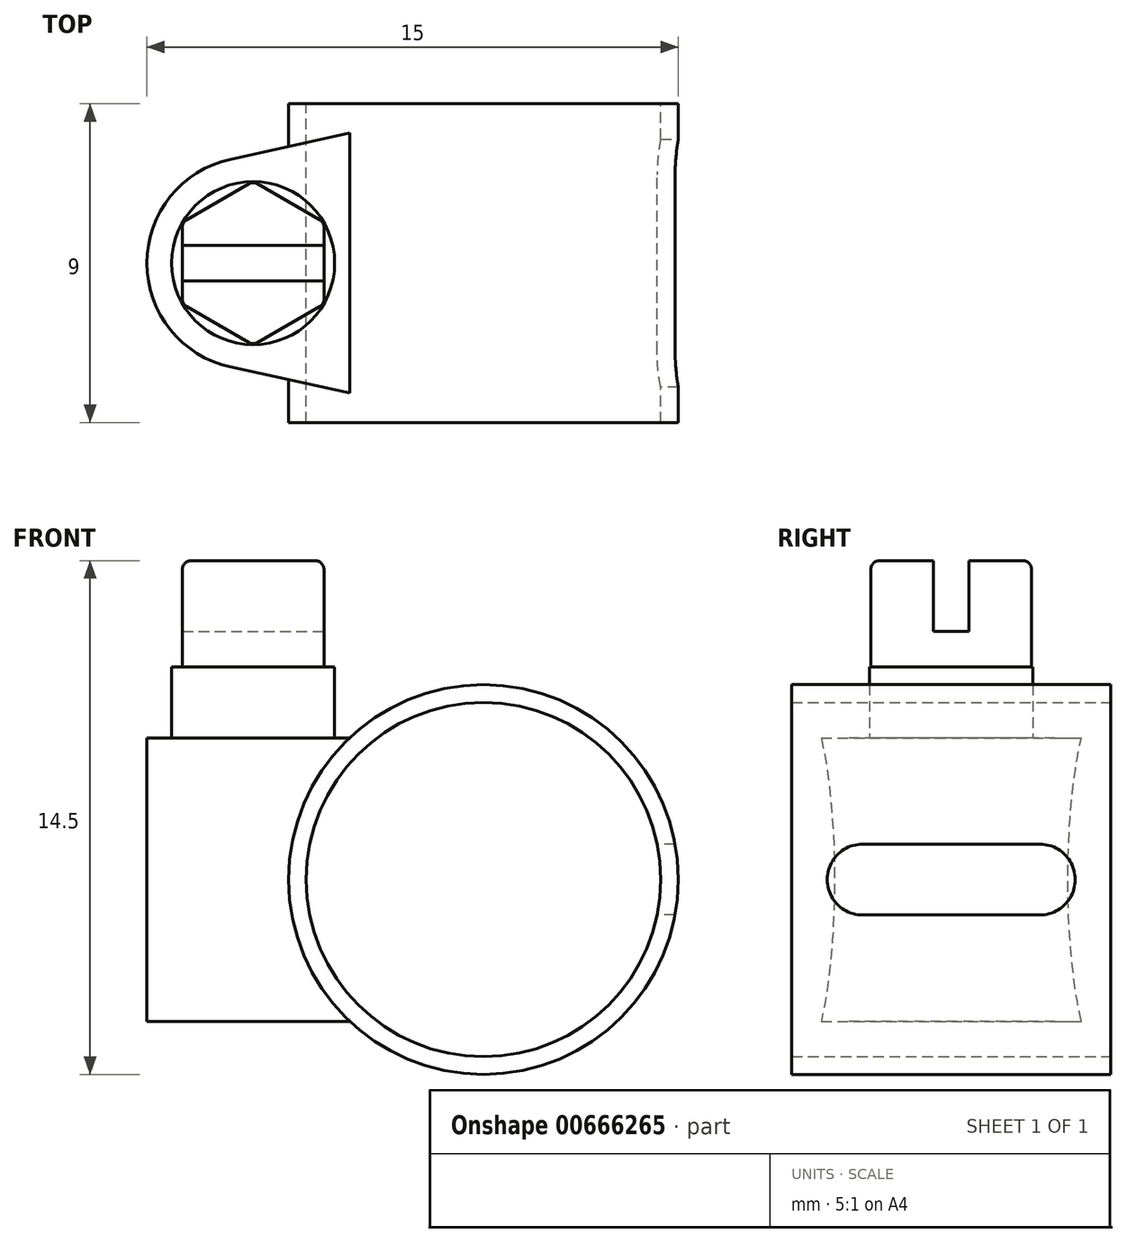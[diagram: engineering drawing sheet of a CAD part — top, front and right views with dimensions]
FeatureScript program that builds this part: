
annotation { "Feature Type Name" : "Feature", "Feature Type Description" : "" }
export const myFeature = defineFeature(function(context is Context, id is Id, definition is map)
    precondition{}
    {
        {
            var Q0;
            Q0=qCreatedBy(makeId("Front.planeOp"),FACE);
            var sketch = newSketch(context, id + "F0", { "sketchPlane" : qUnion([Q0])});
            skCircle(sketch, "E0", {"center": v(0, 0) * mm, "radius": 5.5 * mm});
            skCircle(sketch, "E1", {"center": v(0, 0) * mm, "radius": 5 * mm, "construction": true});
            skSolve(sketch);
        }
        {
            var Q0;
            Q0 = qSketchRegion(id + "F0", true);
            extrude(context, id + "F1", {"entities" : qUnion([Q0]), "depth" : 9 * mm, "offsetDistance" : 25 * mm, "symmetric" : true});
        }
        {
            var Q0;
            Q0=qCreatedBy(makeId("Top.planeOp"),FACE);
            var sketch = newSketch(context, id + "F2", { "sketchPlane" : qUnion([Q0])});
            skArc(sketch, "E2", {"start": v(-7.14, 2.93) * mm, "mid": v(-9.5, 0) * mm, "end": v(-7.14, -2.93) * mm});
            skLineSegment(sketch, "E3", {"start": v(-7.14, 2.93) * mm, "end": v(0, 4.5) * mm});
            skLineSegment(sketch, "E4", {"start": v(0, 4.5) * mm, "end": v(0, -4.5) * mm});
            skLineSegment(sketch, "E5", {"start": v(0, -4.5) * mm, "end": v(-7.14, -2.93) * mm});
            skSolve(sketch);
        }
        {
            var Q0;
            Q0 = qSketchRegion(id + "F2", true);
            extrude(context, id + "F3", {"entities" : qUnion([Q0]), "operationType" : NewBodyOperationType.ADD, "depth" : 8 * mm, "offsetDistance" : 25 * mm, "symmetric" : true});
        }
        {
            var Q0;
            Q0=makeQuery(id+"F3.opExtrude","CAP_FACE",FACE,{"disambiguationData":[OSD([sQuery(id+"F2.wireOp",EDGE,"E2"),sQuery(id+"F2.wireOp",EDGE,"E3"),sQuery(id+"F2.wireOp",EDGE,"E4"),sQuery(id+"F2.wireOp",EDGE,"E5")])],"isStart":false});
            var sketch = newSketch(context, id + "F4", { "sketchPlane" : qUnion([Q0])});
            skCircle(sketch, "E6.cCircle", {"center": v(-6.5, 0) * mm, "radius": 2 * mm, "construction": true});
            skLineSegment(sketch, "E6.0", {"start": v(-8.5, -1.15) * mm, "end": v(-8.5, 1.15) * mm});
            skLineSegment(sketch, "E6.1", {"start": v(-8.5, 1.15) * mm, "end": v(-6.5, 2.3) * mm});
            skLineSegment(sketch, "E6.2", {"start": v(-6.5, 2.3) * mm, "end": v(-4.5, 1.15) * mm});
            skLineSegment(sketch, "E6.3", {"start": v(-4.5, 1.15) * mm, "end": v(-4.5, -1.15) * mm});
            skLineSegment(sketch, "E6.4", {"start": v(-4.5, -1.15) * mm, "end": v(-6.5, -2.3) * mm});
            skLineSegment(sketch, "E6.5", {"start": v(-6.5, -2.3) * mm, "end": v(-8.5, -1.15) * mm});
            skPoint(sketch, "E6.0.midPoint", {"position": v(-8.5, 0) * mm});
            skSolve(sketch);
        }
        {
            var Q0;
            Q0 = qSketchRegion(id + "F4", true);
            extrude(context, id + "F5", {"entities" : qUnion([Q0]), "operationType" : NewBodyOperationType.ADD, "depth" : 5 * mm, "offsetDistance" : 25 * mm});
        }
        {
            var Q0;
            Q0=makeQuery(id+"F1.opExtrude","CAP_FACE",FACE,{"disambiguationData":[OSD([sQuery(id+"F0.wireOp",EDGE,"E0")])],"isStart":true});
            var sketch = newSketch(context, id + "F6", { "sketchPlane" : qUnion([Q0])});
            skCircle(sketch, "E7", {"center": v(0, 0) * mm, "radius": 5 * mm});
            skSolve(sketch);
        }
        {
            var Q0;
            Q0 = qSketchRegion(id + "F6", true);
            extrude(context, id + "F7", {"entities" : qUnion([Q0]), "operationType" : NewBodyOperationType.REMOVE, "endBound" : BoundingType.THROUGH_ALL, "oppositeDirection" : true, "depth" : 25 * mm, "offsetDistance" : 25 * mm});
        }
        {
            var Q0;
            Q0=makeQuery(id+"F5.opExtrude","CAP_FACE",FACE,{"disambiguationData":[OSD([sQuery(id+"F4.wireOp",EDGE,"E6.0"),sQuery(id+"F4.wireOp",EDGE,"E6.1"),sQuery(id+"F4.wireOp",EDGE,"E6.2"),sQuery(id+"F4.wireOp",EDGE,"E6.3"),sQuery(id+"F4.wireOp",EDGE,"E6.4"),sQuery(id+"F4.wireOp",EDGE,"E6.5")])],"isStart":false});
            var sketch = newSketch(context, id + "F8", { "sketchPlane" : qUnion([Q0])});
            skLineSegment(sketch, "E8.bottom", {"start": v(-8.5, 0.5) * mm, "end": v(-4.5, 0.5) * mm});
            skLineSegment(sketch, "E8.top", {"start": v(-8.5, -0.5) * mm, "end": v(-4.5, -0.5) * mm});
            skLineSegment(sketch, "E8.left", {"start": v(-8.5, 0.5) * mm, "end": v(-8.5, -0.5) * mm});
            skLineSegment(sketch, "E8.right", {"start": v(-4.5, 0.5) * mm, "end": v(-4.5, -0.5) * mm});
            skPoint(sketch, "E8.middle", {"position": v(-6.5, 0) * mm});
            skSolve(sketch);
        }
        {
            var Q0;
            Q0 = qSketchRegion(id + "F8", true);
            extrude(context, id + "F9", {"entities" : qUnion([Q0]), "operationType" : NewBodyOperationType.REMOVE, "oppositeDirection" : true, "depth" : 2 * mm, "offsetDistance" : 25 * mm});
        }
        {
            var Q0;
            Q0=makeQuery(id+"F5.opExtrude","SWEPT_EDGE",EDGE,{"disambiguationData":[OSD([sQuery(id+"F4.wireOp",EDGE,"E6.0"),sQuery(id+"F4.wireOp",EDGE,"E6.1")])]});
            var Q1;
            Q1=makeQuery(id+"F5.opExtrude","SWEPT_EDGE",EDGE,{"disambiguationData":[OSD([sQuery(id+"F4.wireOp",EDGE,"E6.1"),sQuery(id+"F4.wireOp",EDGE,"E6.2")])]});
            var Q2;
            Q2=makeQuery(id+"F5.opExtrude","SWEPT_EDGE",EDGE,{"disambiguationData":[OSD([sQuery(id+"F4.wireOp",EDGE,"E6.0"),sQuery(id+"F4.wireOp",EDGE,"E6.5")])]});
            var Q3;
            Q3=makeQuery(id+"F5.opExtrude","SWEPT_EDGE",EDGE,{"disambiguationData":[OSD([sQuery(id+"F4.wireOp",EDGE,"E6.4"),sQuery(id+"F4.wireOp",EDGE,"E6.5")])]});
            var Q4;
            Q4=makeQuery(id+"F5.opExtrude","SWEPT_EDGE",EDGE,{"disambiguationData":[OSD([sQuery(id+"F4.wireOp",EDGE,"E6.3"),sQuery(id+"F4.wireOp",EDGE,"E6.4")])]});
            var Q5;
            Q5=makeQuery(id+"F5.opExtrude","SWEPT_EDGE",EDGE,{"disambiguationData":[OSD([sQuery(id+"F4.wireOp",EDGE,"E6.2"),sQuery(id+"F4.wireOp",EDGE,"E6.3")])]});
            var Q6;
            Q6=makeQuery(id+"F5.opExtrude","CAP_EDGE",EDGE,{"disambiguationData":[OSD([sQuery(id+"F4.wireOp",EDGE,"E6.2")])],"isStart":false});
            var Q7;
            Q7=makeQuery(id+"F5.opExtrude","CAP_EDGE",EDGE,{"disambiguationData":[OSD([sQuery(id+"F4.wireOp",EDGE,"E6.1")])],"isStart":false});
            var Q8;
            {var subQ0=sQuery(id+"F4.wireOp",EDGE,"E6.0");var subQ1=sQuery(id+"F4.wireOp",EDGE,"E6.1");Q8=makeQuery(id+"F9.boolean.opBoolean","SPLIT",EDGE,{"disambiguationData":[TD([makeQuery(id+"F5.opExtrude","SWEPT_FACE",FACE,{"disambiguationData":[OSD([subQ1])]})])],"derivedFrom":makeQuery(id+"F5.opExtrude","CAP_EDGE",EDGE,{"disambiguationData":[OSD([subQ0])],"isStart":false})});}
            var Q9;
            {var subQ0=sQuery(id+"F4.wireOp",EDGE,"E6.3");var subQ1=sQuery(id+"F4.wireOp",EDGE,"E6.2");Q9=makeQuery(id+"F9.boolean.opBoolean","SPLIT",EDGE,{"disambiguationData":[TD([makeQuery(id+"F5.opExtrude","SWEPT_FACE",FACE,{"disambiguationData":[OSD([subQ1])]})])],"derivedFrom":makeQuery(id+"F5.opExtrude","CAP_EDGE",EDGE,{"disambiguationData":[OSD([subQ0])],"isStart":false})});}
            var Q10;
            {var subQ0=sQuery(id+"F4.wireOp",EDGE,"E6.0");var subQ1=sQuery(id+"F4.wireOp",EDGE,"E6.5");Q10=makeQuery(id+"F9.boolean.opBoolean","SPLIT",EDGE,{"disambiguationData":[TD([makeQuery(id+"F5.opExtrude","SWEPT_FACE",FACE,{"disambiguationData":[OSD([subQ1])]})])],"derivedFrom":makeQuery(id+"F5.opExtrude","CAP_EDGE",EDGE,{"disambiguationData":[OSD([subQ0])],"isStart":false})});}
            var Q11;
            Q11=makeQuery(id+"F5.opExtrude","CAP_EDGE",EDGE,{"disambiguationData":[OSD([sQuery(id+"F4.wireOp",EDGE,"E6.5")])],"isStart":false});
            var Q12;
            {var subQ0=sQuery(id+"F4.wireOp",EDGE,"E6.4");var subQ1=sQuery(id+"F4.wireOp",EDGE,"E6.3");Q12=makeQuery(id+"F9.boolean.opBoolean","SPLIT",EDGE,{"disambiguationData":[TD([makeQuery(id+"F5.opExtrude","SWEPT_FACE",FACE,{"disambiguationData":[OSD([subQ0])]})])],"derivedFrom":makeQuery(id+"F5.opExtrude","CAP_EDGE",EDGE,{"disambiguationData":[OSD([subQ1])],"isStart":false})});}
            var Q13;
            Q13=makeQuery(id+"F5.opExtrude","CAP_EDGE",EDGE,{"disambiguationData":[OSD([sQuery(id+"F4.wireOp",EDGE,"E6.4")])],"isStart":false});
            fillet(context, id + "F10", {"entities" : qUnion([Q0, Q1, Q2, Q3, Q4, Q5, Q6, Q7, Q8, Q9, Q10, Q11, Q12, Q13]), "radius" : 0.25 * mm, "tangentPropagation" : true, "allowEdgeOverflow" : false});
        }
        {
            var Q0;
            Q0=makeQuery(id+"F3.opExtrude","CAP_FACE",FACE,{"disambiguationData":[OSD([sQuery(id+"F2.wireOp",EDGE,"E2"),sQuery(id+"F2.wireOp",EDGE,"E3"),sQuery(id+"F2.wireOp",EDGE,"E4"),sQuery(id+"F2.wireOp",EDGE,"E5")])],"isStart":false});
            var sketch = newSketch(context, id + "F11", { "sketchPlane" : qUnion([Q0])});
            skCircle(sketch, "E9", {"center": v(-6.5, 0) * mm, "radius": 2.3 * mm});
            skSolve(sketch);
        }
        {
            var Q0;
            Q0 = qSketchRegion(id + "F11", true);
            extrude(context, id + "F12", {"entities" : qUnion([Q0]), "operationType" : NewBodyOperationType.ADD, "depth" : 2 * mm, "offsetDistance" : 25 * mm});
        }
        {
            var Q0;
            Q0=qCreatedBy(makeId("Right.planeOp"),FACE);
            var sketch = newSketch(context, id + "F13", { "sketchPlane" : qUnion([Q0])});
            skLineSegment(sketch, "E10.bottom", {"start": v(-3.5, 1) * mm, "end": v(3.5, 1) * mm});
            skLineSegment(sketch, "E10.top", {"start": v(-3.5, -1) * mm, "end": v(3.5, -1) * mm});
            skLineSegment(sketch, "E10.left", {"start": v(-3.5, 1) * mm, "end": v(-3.5, -1) * mm});
            skLineSegment(sketch, "E10.right", {"start": v(3.5, 1) * mm, "end": v(3.5, -1) * mm});
            skPoint(sketch, "E10.middle", {"position": v(0, 0) * mm});
            skSolve(sketch);
        }
        {
            var Q0;
            Q0 = qSketchRegion(id + "F13", true);
            var Q1;
            Q1=makeQuery(id+"F1.opExtrude","SWEPT_FACE",FACE,{"disambiguationData":[OSD([sQuery(id+"F0.wireOp",EDGE,"E0")])]});
            extrude(context, id + "F14", {"entities" : qUnion([Q0]), "operationType" : NewBodyOperationType.REMOVE, "endBound" : BoundingType.UP_TO_SURFACE, "depth" : 25 * mm, "endBoundEntityFace" : qUnion([Q1]), "offsetDistance" : 25 * mm});
        }
        {
            var Q0;
            Q0=makeQuery(id+"F14.boolean.opBoolean","COPY",EDGE,{"derivedFrom":makeQuery(id+"F14.opExtrude","SWEPT_EDGE",EDGE,{"disambiguationData":[OSD([sQuery(id+"F13.wireOp",EDGE,"E10.bottom"),sQuery(id+"F13.wireOp",EDGE,"E10.left")])]})});
            var Q1;
            Q1=makeQuery(id+"F14.boolean.opBoolean","COPY",EDGE,{"derivedFrom":makeQuery(id+"F14.opExtrude","SWEPT_EDGE",EDGE,{"disambiguationData":[OSD([sQuery(id+"F13.wireOp",EDGE,"E10.top"),sQuery(id+"F13.wireOp",EDGE,"E10.left")])]})});
            var Q2;
            Q2=makeQuery(id+"F14.boolean.opBoolean","COPY",EDGE,{"derivedFrom":makeQuery(id+"F14.opExtrude","SWEPT_EDGE",EDGE,{"disambiguationData":[OSD([sQuery(id+"F13.wireOp",EDGE,"E10.bottom"),sQuery(id+"F13.wireOp",EDGE,"E10.right")])]})});
            var Q3;
            Q3=makeQuery(id+"F14.boolean.opBoolean","COPY",EDGE,{"derivedFrom":makeQuery(id+"F14.opExtrude","SWEPT_EDGE",EDGE,{"disambiguationData":[OSD([sQuery(id+"F13.wireOp",EDGE,"E10.top"),sQuery(id+"F13.wireOp",EDGE,"E10.right")])]})});
            fillet(context, id + "F15", {"entities" : qUnion([Q0, Q1, Q2, Q3]), "radius" : 1 * mm, "tangentPropagation" : true, "allowEdgeOverflow" : false});
        }
    });
